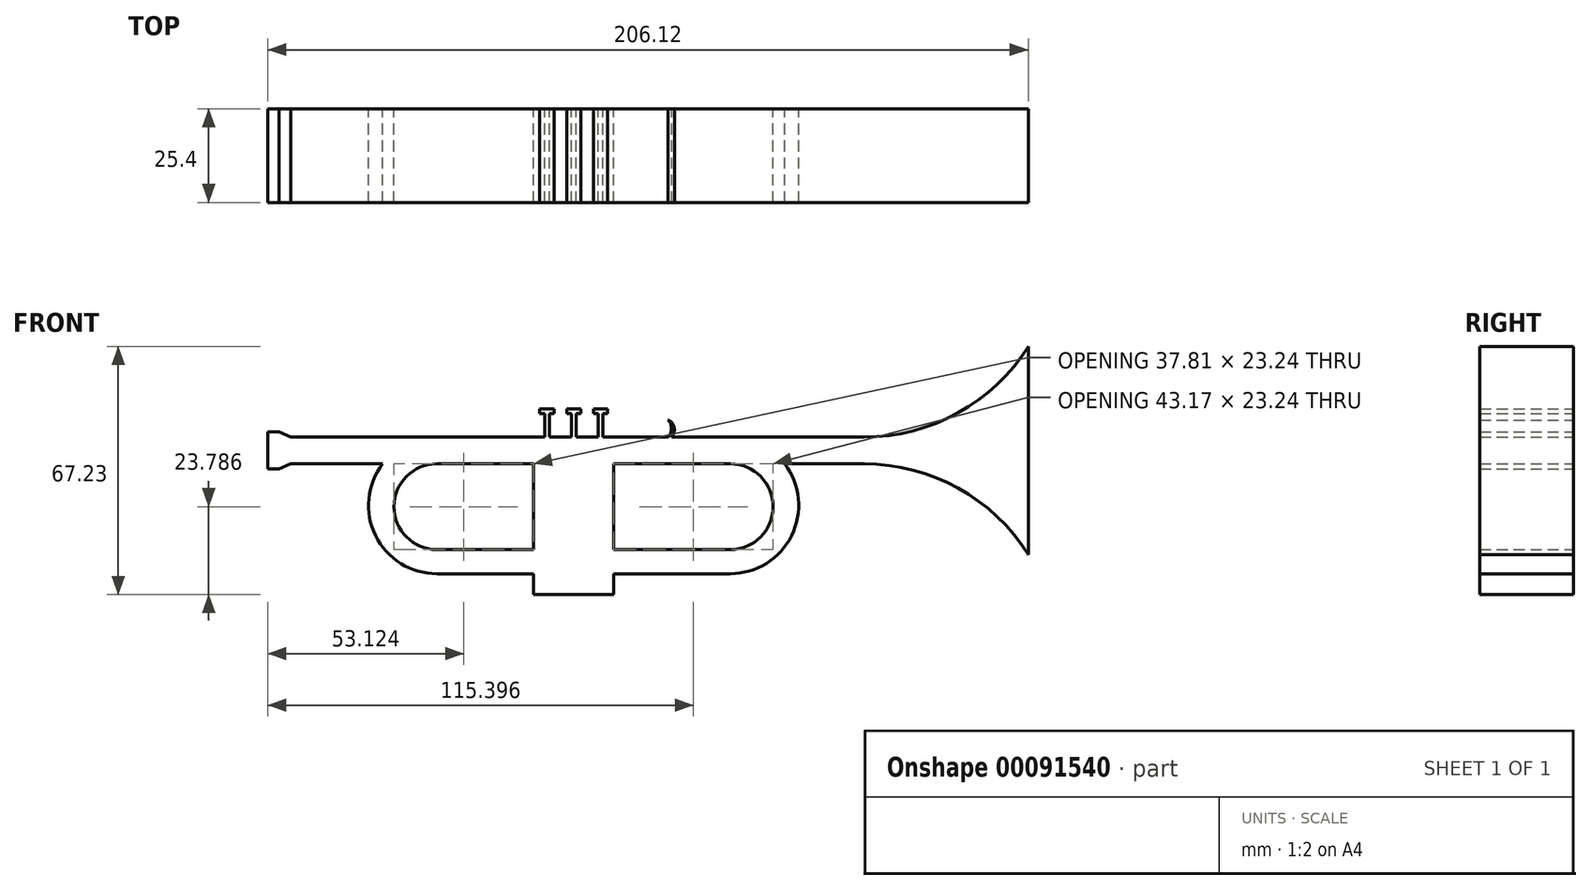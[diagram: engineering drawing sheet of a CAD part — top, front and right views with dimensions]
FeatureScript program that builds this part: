
annotation { "Feature Type Name" : "Feature", "Feature Type Description" : "" }
export const myFeature = defineFeature(function(context is Context, id is Id, definition is map)
    precondition{}
    {
        {
            var Q0;
            Q0=qCreatedBy(makeId("Front.planeOp"),FACE);
            var sketch = newSketch(context, id + "F0", { "sketchPlane" : qUnion([Q0])});
            skArc(sketch, "E0", {"start": v(79.52, 15.98) * mm, "mid": v(91.14, 27.6) * mm, "end": v(79.52, 39.22) * mm});
            skArc(sketch, "E1", {"start": v(79.52, 9.44) * mm, "mid": v(98.04, 27.96) * mm, "end": v(79.52, 46.48) * mm});
            skArc(sketch, "E2", {"start": v(0, 39.22) * mm, "mid": v(-11.62, 27.6) * mm, "end": v(0, 15.98) * mm});
            skArc(sketch, "E3", {"start": v(0, 46.48) * mm, "mid": v(-18.52, 27.96) * mm, "end": v(0, 9.44) * mm});
            skLineSegment(sketch, "E4.bottom", {"start": v(79.52, 46.48) * mm, "end": v(115.83, 46.48) * mm});
            skLineSegment(sketch, "E5.top", {"start": v(115.83, 46.48) * mm, "end": v(-37.18, 46.48) * mm});
            skLineSegment(sketch, "E5.right", {"start": v(-37.18, 39.22) * mm, "end": v(-37.18, 46.48) * mm});
            skLineSegment(sketch, "E6", {"start": v(-37.18, 39.22) * mm, "end": v(-14.7, 39.22) * mm});
            skLineSegment(sketch, "E7", {"start": v(115.83, 39.22) * mm, "end": v(94.22, 39.22) * mm});
            skLineSegment(sketch, "E8.bottom", {"start": v(26.19, 46.48) * mm, "end": v(55.23, 46.48) * mm});
            skLineSegment(sketch, "E8.left", {"start": v(26.19, 46.48) * mm, "end": v(26.19, 3.81) * mm});
            skPoint(sketch, "E9.startSnap0", {"position": v(39.76, 39.22) * mm});
            skLineSegment(sketch, "E10", {"start": v(-37.18, 46.48) * mm, "end": v(-39.62, 46.48) * mm});
            skLineSegment(sketch, "E11", {"start": v(-39.62, 46.48) * mm, "end": v(-42.77, 47.9) * mm});
            skLineSegment(sketch, "E12", {"start": v(-42.77, 47.9) * mm, "end": v(-45.84, 47.9) * mm});
            skLineSegment(sketch, "E13", {"start": v(-45.84, 47.9) * mm, "end": v(-42.77, 47.9) * mm});
            skLineSegment(sketch, "E14", {"start": v(-37.18, 39.22) * mm, "end": v(-39.62, 39.22) * mm});
            skLineSegment(sketch, "E15.MirrorCS", {"start": v(-39.62, 39.22) * mm, "end": v(-42.77, 37.79) * mm});
            skLineSegment(sketch, "E16.MirrorCS", {"start": v(-45.84, 37.79) * mm, "end": v(-42.77, 37.79) * mm});
            skLineSegment(sketch, "E17", {"start": v(-45.84, 47.9) * mm, "end": v(-45.84, 37.79) * mm});
            skLineSegment(sketch, "E18", {"start": v(-39.62, 46.48) * mm, "end": v(-39.62, 39.22) * mm});
            skLineSegment(sketch, "E19", {"start": v(-42.77, 37.79) * mm, "end": v(-42.77, 47.9) * mm});
            skLineSegment(sketch, "E20", {"start": v(40.71, 46.48) * mm, "end": v(26.19, 46.48) * mm});
            skLineSegment(sketch, "E21", {"start": v(33.45, 46.48) * mm, "end": v(40.71, 46.48) * mm});
            skLineSegment(sketch, "E22", {"start": v(40.71, 46.48) * mm, "end": v(55.23, 46.48) * mm});
            skLineSegment(sketch, "E23", {"start": v(40.71, 46.48) * mm, "end": v(47.97, 46.48) * mm});
            skLineSegment(sketch, "E24", {"start": v(47.97, 46.48) * mm, "end": v(47.97, 3.81) * mm});
            skLineSegment(sketch, "E25", {"start": v(33.45, 46.48) * mm, "end": v(33.45, 3.81) * mm});
            skLineSegment(sketch, "E26", {"start": v(0, 39.22) * mm, "end": v(26.19, 39.22) * mm});
            skLineSegment(sketch, "E27", {"start": v(55.23, 39.22) * mm, "end": v(79.52, 39.22) * mm});
            skLineSegment(sketch, "E28", {"start": v(40.71, 46.48) * mm, "end": v(40.71, 3.81) * mm});
            skLineSegment(sketch, "E29", {"start": v(0, 15.98) * mm, "end": v(26.19, 15.98) * mm});
            skLineSegment(sketch, "E30", {"start": v(26.19, 15.98) * mm, "end": v(26.19, 9.44) * mm});
            skLineSegment(sketch, "E31", {"start": v(26.19, 9.44) * mm, "end": v(0, 9.44) * mm});
            skLineSegment(sketch, "E32", {"start": v(79.52, 9.44) * mm, "end": v(55.23, 9.44) * mm});
            skLineSegment(sketch, "E33", {"start": v(79.52, 15.98) * mm, "end": v(55.23, 15.98) * mm});
            skLineSegment(sketch, "E34", {"start": v(160.28, 42.85) * mm, "end": v(160.28, 71.04) * mm});
            skLineSegment(sketch, "E35", {"start": v(160.28, 71.04) * mm, "end": v(160.28, 57.16) * mm});
            skLineSegment(sketch, "E36.MirrorCS", {"start": v(160.28, 14.66) * mm, "end": v(160.28, 42.85) * mm});
            skLineSegment(sketch, "E37", {"start": v(160.28, 46.48) * mm, "end": v(160.28, 39.22) * mm});
            skArc(sketch, "E38", {"start": v(115.83, 46.48) * mm, "mid": v(141.22, 53.03) * mm, "end": v(160.28, 71.04) * mm});
            skArc(sketch, "E39", {"start": v(160.28, 14.66) * mm, "mid": v(141.22, 32.67) * mm, "end": v(115.83, 39.22) * mm});
            skLineSegment(sketch, "E40", {"start": v(26.19, 46.48) * mm, "end": v(33.45, 46.48) * mm});
            skLineSegment(sketch, "E41", {"start": v(47.97, 46.48) * mm, "end": v(40.71, 46.48) * mm});
            skLineSegment(sketch, "E42", {"start": v(29.82, 46.48) * mm, "end": v(29.18, 46.48) * mm});
            skLineSegment(sketch, "E43", {"start": v(29.18, 46.48) * mm, "end": v(29.82, 46.48) * mm});
            skLineSegment(sketch, "E44", {"start": v(29.82, 46.48) * mm, "end": v(30.45, 46.48) * mm});
            skLineSegment(sketch, "E45", {"start": v(30.45, 46.48) * mm, "end": v(29.18, 46.48) * mm});
            skLineSegment(sketch, "E46.bottom", {"start": v(29.18, 46.48) * mm, "end": v(30.45, 46.48) * mm});
            skLineSegment(sketch, "E46.left", {"start": v(29.18, 46.48) * mm, "end": v(29.18, 52.8) * mm});
            skLineSegment(sketch, "E46.right", {"start": v(30.45, 46.48) * mm, "end": v(30.45, 52.8) * mm});
            skLineSegment(sketch, "E47.MirrorCS", {"start": v(36.45, 46.48) * mm, "end": v(36.45, 52.8) * mm});
            skLineSegment(sketch, "E48.MirrorCS", {"start": v(37.71, 52.8) * mm, "end": v(36.45, 52.8) * mm});
            skLineSegment(sketch, "E49.MirrorCS", {"start": v(37.71, 46.48) * mm, "end": v(37.71, 52.8) * mm});
            skLineSegment(sketch, "E50.MirrorCS", {"start": v(43.7, 46.48) * mm, "end": v(43.7, 52.8) * mm});
            skLineSegment(sketch, "E51.MirrorCS", {"start": v(44.97, 46.48) * mm, "end": v(44.97, 52.8) * mm});
            skLineSegment(sketch, "E52.MirrorCS", {"start": v(43.7, 52.8) * mm, "end": v(44.97, 52.8) * mm});
            skLineSegment(sketch, "E53", {"start": v(26.19, 3.81) * mm, "end": v(47.97, 3.81) * mm});
            skLineSegment(sketch, "E54", {"start": v(55.23, 15.98) * mm, "end": v(47.97, 15.98) * mm});
            skLineSegment(sketch, "E55", {"start": v(55.23, 9.44) * mm, "end": v(47.97, 9.44) * mm});
            skLineSegment(sketch, "E56", {"start": v(55.23, 39.22) * mm, "end": v(47.97, 39.22) * mm});
            skLineSegment(sketch, "E57.top", {"start": v(29.18, 54.08) * mm, "end": v(30.45, 54.08) * mm});
            skLineSegment(sketch, "E58.bottom", {"start": v(30.45, 54.08) * mm, "end": v(31.72, 54.08) * mm});
            skLineSegment(sketch, "E58.top", {"start": v(30.45, 52.8) * mm, "end": v(31.72, 52.8) * mm});
            skLineSegment(sketch, "E58.right", {"start": v(31.72, 54.08) * mm, "end": v(31.72, 52.8) * mm});
            skLineSegment(sketch, "E59", {"start": v(29.18, 54.08) * mm, "end": v(27.9, 54.08) * mm});
            skLineSegment(sketch, "E60", {"start": v(27.9, 54.08) * mm, "end": v(27.9, 52.8) * mm});
            skLineSegment(sketch, "E61", {"start": v(27.9, 52.8) * mm, "end": v(29.18, 52.8) * mm});
            skLineSegment(sketch, "E62", {"start": v(29.18, 52.8) * mm, "end": v(30.45, 52.8) * mm});
            skLineSegment(sketch, "E63.MirrorCS", {"start": v(36.45, 52.8) * mm, "end": v(35.18, 52.8) * mm});
            skLineSegment(sketch, "E64.MirrorCS", {"start": v(39, 52.8) * mm, "end": v(37.71, 52.8) * mm});
            skLineSegment(sketch, "E65.MirrorCS", {"start": v(39, 54.08) * mm, "end": v(39, 52.8) * mm});
            skLineSegment(sketch, "E66.MirrorCS", {"start": v(37.71, 54.08) * mm, "end": v(39, 54.08) * mm});
            skLineSegment(sketch, "E67.MirrorCS", {"start": v(37.71, 54.08) * mm, "end": v(36.45, 54.08) * mm});
            skLineSegment(sketch, "E68.MirrorCS", {"start": v(36.45, 54.08) * mm, "end": v(35.18, 54.08) * mm});
            skLineSegment(sketch, "E69.MirrorCS", {"start": v(35.18, 54.08) * mm, "end": v(35.18, 52.8) * mm});
            skLineSegment(sketch, "E70.MirrorCS", {"start": v(42.43, 52.8) * mm, "end": v(43.7, 52.8) * mm});
            skLineSegment(sketch, "E71.MirrorCS", {"start": v(42.43, 54.08) * mm, "end": v(42.43, 52.8) * mm});
            skLineSegment(sketch, "E72.MirrorCS", {"start": v(43.7, 54.08) * mm, "end": v(42.43, 54.08) * mm});
            skLineSegment(sketch, "E73.MirrorCS", {"start": v(43.7, 54.08) * mm, "end": v(44.97, 54.08) * mm});
            skLineSegment(sketch, "E74.MirrorCS", {"start": v(44.97, 54.08) * mm, "end": v(46.24, 54.08) * mm});
            skLineSegment(sketch, "E75.MirrorCS", {"start": v(46.24, 54.08) * mm, "end": v(46.24, 52.8) * mm});
            skLineSegment(sketch, "E76.MirrorCS", {"start": v(44.97, 52.8) * mm, "end": v(46.24, 52.8) * mm});
            skArc(sketch, "E77", {"start": v(62.7, 46.48) * mm, "mid": v(63.6, 48.8) * mm, "end": v(62.7, 51.11) * mm});
            skArc(sketch, "E78", {"start": v(63.6, 46.48) * mm, "mid": v(64.33, 49.02) * mm, "end": v(62.7, 51.11) * mm});
            skPoint(sketch, "E78.startSnap0", {"position": v(63.6, 48.8) * mm});
            skSolve(sketch);
        }
        {
            var Q0;
            Q0 = qSketchRegion(id + "F0", true);
            extrude(context, id + "F1", {"entities" : qUnion([Q0]), "depth" : 25.4 * mm});
        }
    });
